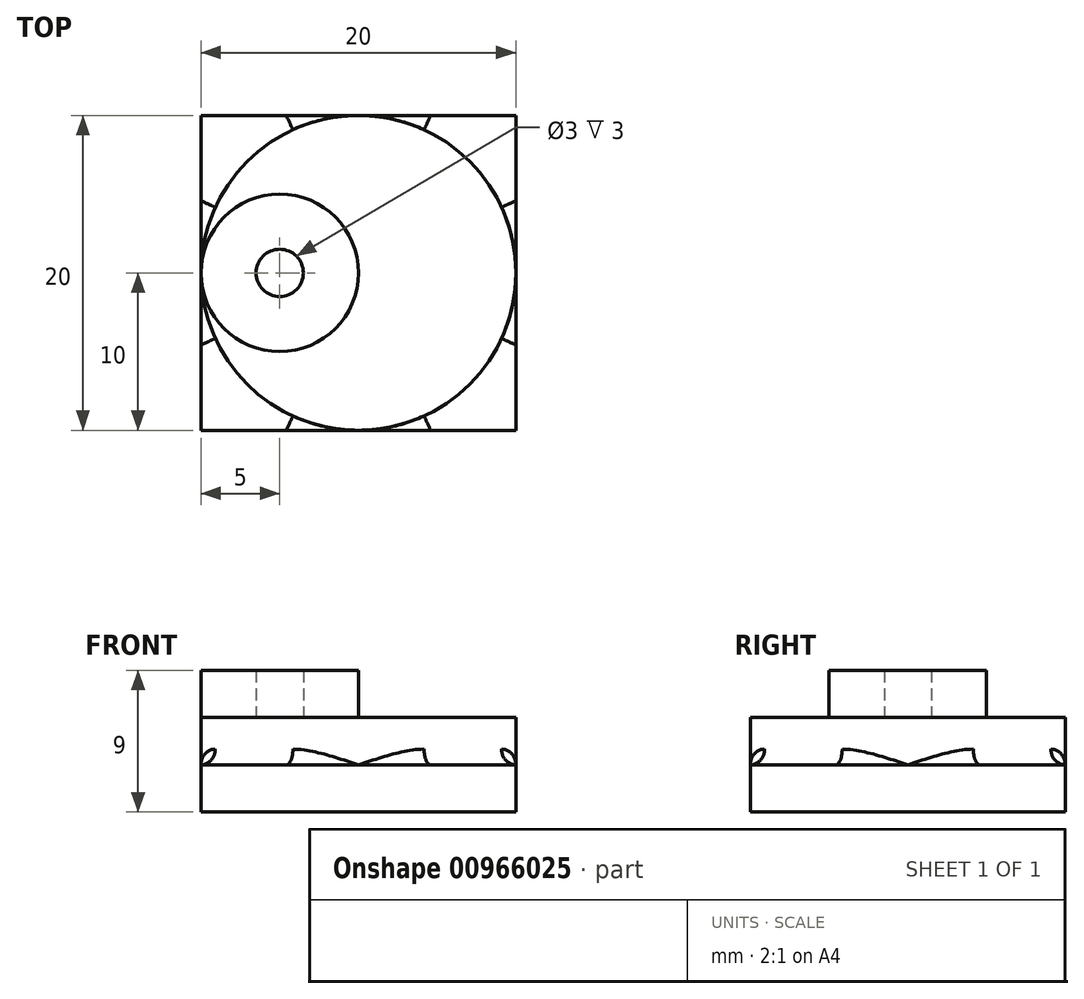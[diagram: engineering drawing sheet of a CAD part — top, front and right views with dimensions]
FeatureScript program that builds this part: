
annotation { "Feature Type Name" : "Feature", "Feature Type Description" : "" }
export const myFeature = defineFeature(function(context is Context, id is Id, definition is map)
    precondition{}
    {
        {
            var Q0;
            Q0=qCreatedBy(makeId("Top.planeOp"),FACE);
            var sketch = newSketch(context, id + "F0", { "sketchPlane" : qUnion([Q0])});
            skLineSegment(sketch, "E0.bottom", {"start": v(0, 0) * mm, "end": v(20, 0) * mm});
            skLineSegment(sketch, "E0.top", {"start": v(0, 20) * mm, "end": v(20, 20) * mm});
            skLineSegment(sketch, "E0.left", {"start": v(0, 0) * mm, "end": v(0, 20) * mm});
            skLineSegment(sketch, "E0.right", {"start": v(20, 0) * mm, "end": v(20, 20) * mm});
            skSolve(sketch);
        }
        {
            var Q0;
            Q0=makeQuery(id+"F0.imprint","IMPRINT",FACE,{"disambiguationData":[TD([[makeQuery(id+"F0.imprint","IMPRINT",EDGE,{"derivedFrom":sQuery(id+"F0.wireOp",EDGE,"E0.bottom")}),1.0]])]});
            extrude(context, id + "F1", {"entities" : qUnion([Q0]), "depth" : 3 * mm, "offsetDistance" : 25 * mm});
        }
        {
            var Q0;
            Q0=makeQuery(id+"F1.opExtrude","CAP_FACE",FACE,{"disambiguationData":[OSD([sQuery(id+"F0.wireOp",EDGE,"E0.bottom"),sQuery(id+"F0.wireOp",EDGE,"E0.top"),sQuery(id+"F0.wireOp",EDGE,"E0.left"),sQuery(id+"F0.wireOp",EDGE,"E0.right")])],"isStart":false});
            var sketch = newSketch(context, id + "F2", { "sketchPlane" : qUnion([Q0])});
            skCircle(sketch, "E1", {"center": v(10, 10) * mm, "radius": 10 * mm});
            skSolve(sketch);
        }
        {
            var Q0;
            {var subQ0=sQuery(id+"F2.wireOp",EDGE,"E1");var subQ1=makeQuery(id+"F2.imprint","INTERSECT",VERTEX,{"derivedFrom":[makeQuery(id+"F1.opExtrude","CAP_EDGE",EDGE,{"disambiguationData":[OSD([sQuery(id+"F0.wireOp",EDGE,"E0.top")])],"isStart":false}),subQ0]});Q0=makeQuery(id+"F2.imprint","IMPRINT",FACE,{"disambiguationData":[TD([[makeQuery(id+"F2.imprint","IMPRINT",EDGE,{"disambiguationData":[TD([[subQ1,1.0]])],"derivedFrom":subQ0}),1.0]])]});}
            extrude(context, id + "F3", {"entities" : qUnion([Q0]), "operationType" : NewBodyOperationType.ADD, "depth" : 3 * mm, "offsetDistance" : 25 * mm});
        }
        {
            var Q0;
            Q0=makeQuery(id+"F3.opExtrude","CAP_FACE",FACE,{"disambiguationData":[OSD([sQuery(id+"F2.wireOp",EDGE,"E1")])],"isStart":false});
            var sketch = newSketch(context, id + "F4", { "sketchPlane" : qUnion([Q0])});
            skCircle(sketch, "E2", {"center": v(5, 10) * mm, "radius": 5 * mm});
            skCircle(sketch, "E3", {"center": v(5, 10) * mm, "radius": 1.5 * mm});
            skSolve(sketch);
        }
        {
            var Q0;
            Q0=makeQuery(id+"F4.imprint","IMPRINT",FACE,{"disambiguationData":[TD([[makeQuery(id+"F4.imprint","IMPRINT",EDGE,{"derivedFrom":sQuery(id+"F4.wireOp",EDGE,"E2")}),1.0]])]});
            extrude(context, id + "F5", {"entities" : qUnion([Q0]), "operationType" : NewBodyOperationType.ADD, "depth" : 3 * mm, "offsetDistance" : 25 * mm});
        }
        {
            var Q0;
            {var subQ0=sQuery(id+"F0.wireOp",EDGE,"E0.bottom");var subQ1=sQuery(id+"F0.wireOp",EDGE,"E0.right");var subQ2=sQuery(id+"F2.wireOp",EDGE,"E1");Q0=makeQuery(id+"F3.boolean.opBoolean","SPLIT",EDGE,{"disambiguationData":[TD([makeQuery(id+"F1.opExtrude","SWEPT_FACE",FACE,{"disambiguationData":[OSD([subQ0])]}),makeQuery(id+"F1.opExtrude","CAP_FACE",FACE,{"disambiguationData":[OSD([subQ0,sQuery(id+"F0.wireOp",EDGE,"E0.top"),sQuery(id+"F0.wireOp",EDGE,"E0.left"),subQ1])],"isStart":false}),makeQuery(id+"F1.opExtrude","SWEPT_FACE",FACE,{"disambiguationData":[OSD([subQ1])]}),makeQuery(id+"F3.opExtrude","SWEPT_FACE",FACE,{"disambiguationData":[OSD([subQ2])]})])],"derivedFrom":makeQuery(id+"F3.opExtrude","CAP_EDGE",EDGE,{"disambiguationData":[OSD([subQ2])],"isStart":true})});}
            var Q1;
            {var subQ0=sQuery(id+"F0.wireOp",EDGE,"E0.bottom");var subQ1=sQuery(id+"F2.wireOp",EDGE,"E1");var subQ2=sQuery(id+"F0.wireOp",EDGE,"E0.left");Q1=makeQuery(id+"F3.boolean.opBoolean","SPLIT",EDGE,{"disambiguationData":[TD([makeQuery(id+"F1.opExtrude","SWEPT_FACE",FACE,{"disambiguationData":[OSD([subQ0])]}),makeQuery(id+"F1.opExtrude","CAP_FACE",FACE,{"disambiguationData":[OSD([subQ0,sQuery(id+"F0.wireOp",EDGE,"E0.top"),subQ2,sQuery(id+"F0.wireOp",EDGE,"E0.right")])],"isStart":false}),makeQuery(id+"F1.opExtrude","SWEPT_FACE",FACE,{"disambiguationData":[OSD([subQ2])]}),makeQuery(id+"F3.opExtrude","SWEPT_FACE",FACE,{"disambiguationData":[OSD([subQ1])]})])],"derivedFrom":makeQuery(id+"F3.opExtrude","CAP_EDGE",EDGE,{"disambiguationData":[OSD([subQ1])],"isStart":true})});}
            var Q2;
            {var subQ0=sQuery(id+"F0.wireOp",EDGE,"E0.right");var subQ1=sQuery(id+"F0.wireOp",EDGE,"E0.top");var subQ2=sQuery(id+"F2.wireOp",EDGE,"E1");Q2=makeQuery(id+"F3.boolean.opBoolean","SPLIT",EDGE,{"disambiguationData":[TD([makeQuery(id+"F1.opExtrude","CAP_FACE",FACE,{"disambiguationData":[OSD([sQuery(id+"F0.wireOp",EDGE,"E0.bottom"),subQ1,sQuery(id+"F0.wireOp",EDGE,"E0.left"),subQ0])],"isStart":false}),makeQuery(id+"F1.opExtrude","SWEPT_FACE",FACE,{"disambiguationData":[OSD([subQ1])]}),makeQuery(id+"F1.opExtrude","SWEPT_FACE",FACE,{"disambiguationData":[OSD([subQ0])]}),makeQuery(id+"F3.opExtrude","SWEPT_FACE",FACE,{"disambiguationData":[OSD([subQ2])]})])],"derivedFrom":makeQuery(id+"F3.opExtrude","CAP_EDGE",EDGE,{"disambiguationData":[OSD([subQ2])],"isStart":true})});}
            var Q3;
            {var subQ0=sQuery(id+"F0.wireOp",EDGE,"E0.left");var subQ1=sQuery(id+"F0.wireOp",EDGE,"E0.top");var subQ2=sQuery(id+"F2.wireOp",EDGE,"E1");Q3=makeQuery(id+"F3.boolean.opBoolean","SPLIT",EDGE,{"disambiguationData":[TD([makeQuery(id+"F1.opExtrude","CAP_FACE",FACE,{"disambiguationData":[OSD([sQuery(id+"F0.wireOp",EDGE,"E0.bottom"),subQ1,subQ0,sQuery(id+"F0.wireOp",EDGE,"E0.right")])],"isStart":false}),makeQuery(id+"F1.opExtrude","SWEPT_FACE",FACE,{"disambiguationData":[OSD([subQ1])]}),makeQuery(id+"F1.opExtrude","SWEPT_FACE",FACE,{"disambiguationData":[OSD([subQ0])]}),makeQuery(id+"F3.opExtrude","SWEPT_FACE",FACE,{"disambiguationData":[OSD([subQ2])]})])],"derivedFrom":makeQuery(id+"F3.opExtrude","CAP_EDGE",EDGE,{"disambiguationData":[OSD([subQ2])],"isStart":true})});}
            fillet(context, id + "F6", {"entities" : qUnion([Q0, Q1, Q2, Q3]), "radius" : 1 * mm, "tangentPropagation" : true, "allowEdgeOverflow" : false});
        }
    });
